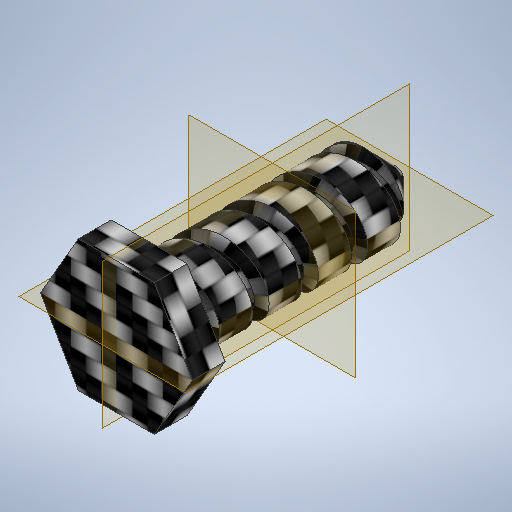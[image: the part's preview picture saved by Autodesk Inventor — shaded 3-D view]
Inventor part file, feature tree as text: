
AUTODESK INVENTOR PART (.ipt)
format: ipt  version: 2025.2 (Build 292293000, 293)  size: 439,808 bytes
history: native  units: mm
features: sketch x3, other x2, extrude x2, chamfer x1
ambient origin geometry x8: Origin, YZ Plane, XZ Plane, XY Plane, X Axis, Y Axis, Z Axis, Center Point
bodies: Body1 (feature_tree)
feature tree (8):
  other  "Sólido1"
  extrude  "Extrusão1"  Depth=15.0mm TaperAngle=0.0deg
  other  "Espiral1"
  chamfer  "Chanfro1"  Distance=4.0mm
  extrude  "Extrusão2"  Depth=2.0mm TaperAngle=0.0deg
  sketch  "Esboço1"  dims[d0=5.0mm d1=15.0mm d2=0.0mm]
  sketch  "Esboço2"  dims[d6=1.0mm]
  sketch  "Esboço5"  dims[d7=0.2mm d8=3.0mm d9=35.0mm d10=10.0mm d11=0.0mm d12=90.0deg d13=90.0deg d14=0.0mm d15=0.0mm d16=2.0mm d17=2.0mm d18=45.0deg d20=4.0mm d21=2.0mm d22=0.0mm d24=0.5mm d25=0.872665mm d26=0.5mm d27=0.872665mm]
